# Revit family: ECJN05LLE
name_source: partatom
category: Lighting Fixtures
revit_build: Autodesk Revit 2014 (Build: 20130308_1515(x64)
units: mm (PartAtom-declared; Revit-internal decimal feet)

## types (1)
- ECJN05LLE
    Apparent Load = 44 VA
    Assembly Code = D5020200
    Color Filter = 16777215
    Connector Description = Lighting Connector
    Default Elevation = 1219.2 mm  [stored 4 ft]
    Description = The Eclipse Junior LED offers all of the power of our popular Eclipse II Wellglass with a 40% reduction in weight. Featuring the latest in LED optics, the Eclipse Jr is a highly energy efficient luminaire for use in Zones 2 and 22.
    Dimming Lamp Color Temperature Shift = <None>
    Emit Shape Visible in Rendering = No
    Emit from Circle Diameter = 50 mm  [stored 0.164042 ft]
    Features = Excellent power savings – save 40% vs a 70W HPS lamp
Strong photometric performance - utlises the latest in LED technology for an instant on crisp white light output
Compact & Lightweight – The lightest out of all the 70W wellglass alternatives. Weighs just 5kg.
Easy to Install – Simple one bolt access for installation
Wide Ambient Temperature Range - -40C to +55C
Allows uplighting – utilises a unique LED optic
Certified for use worldwide – ATEX, IECEx, EAC and INMETRO approvals for use in Zones 2 and 22
Wide Range of Mounting Options available – Pendant, Pole/Column, Medium Bay, Low Bay
    Fixture distribution = Direct
    Glass = Hubbell - Glass
    Height = 535 mm
    Housing Material = Paint - Hubbell - Matte White
    IP Rating = IP66/67
    Inner Length = 200 mm  [stored 0.656168 ft]
    Lamp = LED
    Length = 245 mm  [stored 0.803806 ft]
    Load Classification = Lighting
    Manufacturer = Chalmit
    Model = ECJN/05L/LE
    Mounting = Paint - Hubbell - Light Silver
    Photometric Web File = CHL_ECJN_05L_LE.ies
    Power Factor = 1
    Product Documentation Link = https://hubbellcdn.com
    Product Link = https://www.hubbell.com
    Reflector Finish = Hubbell - White Glass
    Tilt Angle = 90.00°
    URL = https://www.hubbell.com
    Voltage = 120 V
    Warranty = 5 years Warranty
    Wattage Comments = 44W
    Watts = 44 W
    Width = 280 mm
    Wings = Paint - Hubbell - Light Silver

note: [stored X ft] marks values corroborated as IEEE doubles in the binary element streams (Revit-internal decimal feet)

## geometry (parser evidence)
native form markers: Sweep x3
no freeform markers — native parametric forms only
